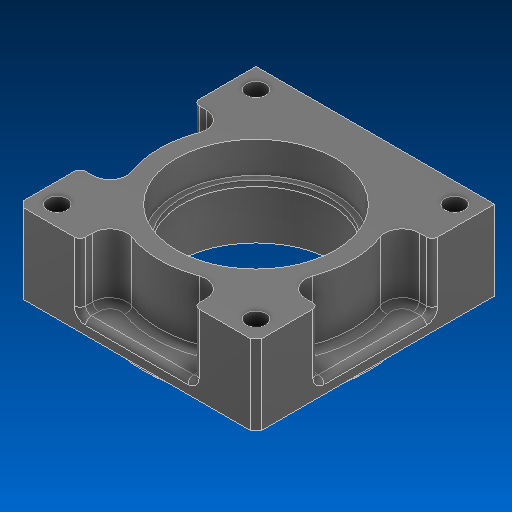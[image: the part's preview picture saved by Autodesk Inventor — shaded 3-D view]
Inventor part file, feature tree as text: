
AUTODESK INVENTOR PART (.ipt)
format: ipt  version: 2022.2 (Build 262287000, 287)  size: 239,104 bytes
history: native  units: in
note: dims shown in document units (in); Inventor stores cm internally (conversion verified against a paired STEP export)
features: chamfer x1
ambient origin geometry x8: Origin, YZ Plane, XZ Plane, XY Plane, X Axis, Y Axis, Z Axis, Center Point
bodies: Solid1 (feature_tree)
feature tree (1):
  chamfer  "Chamfer2"  [1 undecoded]
note: 1 required parameter value undecoded (feature->parameter linkage not recoverable at this tier; creation-order binding heuristic only, values carry confidence <= 0.55)
